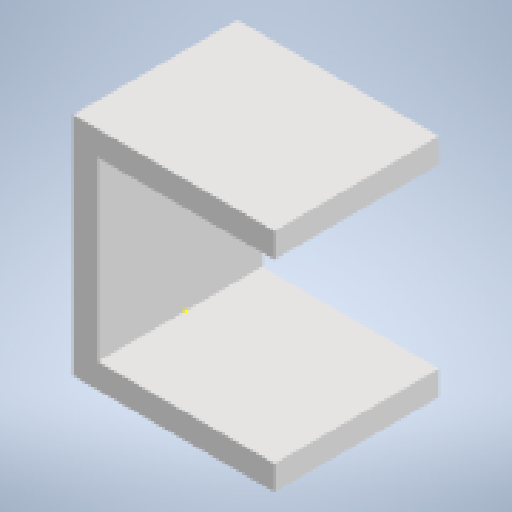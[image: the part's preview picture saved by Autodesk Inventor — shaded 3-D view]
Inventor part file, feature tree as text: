
AUTODESK INVENTOR PART (.ipt)
format: ipt  version: 2023 (Build 270158000, 158)  size: 141,312 bytes
history: native  units: mm
features: reference x6, other x5, sketch x2, extrude x2
ambient origin geometry x8: Origin, YZ Plane, XZ Plane, XY Plane, X Axis, Y Axis, Z Axis, Center Point
bodies: Body1 (feature_tree)
feature tree (15):
  other  "Твердое тело1"
  sketch  "Эскиз1"
  other  "РабПлоскость1"
  extrude  "Выдавливание1"  Depth=43.0mm
  extrude  "Выдавливание2"  Depth=43.0mm
  reference  "Ссылка1"
  reference  "Ссылка2"
  reference  "Ссылка3"
  reference  "Ссылка4"
  sketch  "Эскиз3"
  reference  "Ссылка5"
  reference  "Ссылка6"
  other  "Сборка1"
  other  "17HM15-0904S:1"
  other  "nema17_top_40mm___ __________4"
